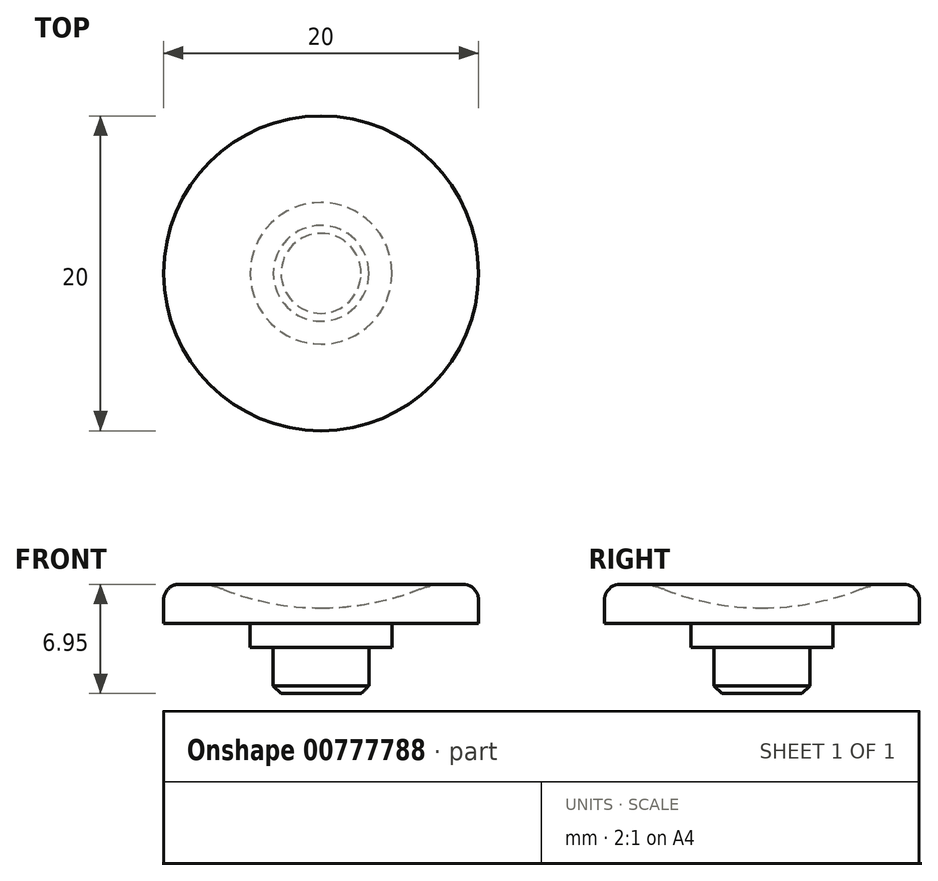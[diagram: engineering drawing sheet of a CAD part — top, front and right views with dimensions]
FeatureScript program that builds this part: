
annotation { "Feature Type Name" : "Feature", "Feature Type Description" : "" }
export const myFeature = defineFeature(function(context is Context, id is Id, definition is map)
    precondition{}
    {
        {
            var Q0;
            Q0=qCreatedBy(makeId("Front.planeOp"),FACE);
            var sketch = newSketch(context, id + "F0", { "sketchPlane" : qUnion([Q0])});
            skLineSegment(sketch, "E0", {"start": v(0, 0) * mm, "end": v(3.04, 0) * mm});
            skLineSegment(sketch, "E1", {"start": v(3.04, 0) * mm, "end": v(3.04, 2.95) * mm});
            skLineSegment(sketch, "E2", {"start": v(3.04, 2.95) * mm, "end": v(4.5, 2.95) * mm});
            skLineSegment(sketch, "E3", {"start": v(4.5, 2.95) * mm, "end": v(4.5, 4.45) * mm});
            skLineSegment(sketch, "E4", {"start": v(0, 0) * mm, "end": v(0, 5.45) * mm});
            skLineSegment(sketch, "E5", {"start": v(4.5, 4.45) * mm, "end": v(10, 4.45) * mm});
            skLineSegment(sketch, "E6", {"start": v(10, 4.45) * mm, "end": v(10, 6.95) * mm});
            skLineSegment(sketch, "E7", {"start": v(10, 6.95) * mm, "end": v(7, 6.95) * mm});
            skArc(sketch, "E8", {"start": v(0, 5.45) * mm, "mid": v(3.58, 5.83) * mm, "end": v(7, 6.95) * mm});
            skLineSegment(sketch, "E9", {"start": v(0, 10.08) * mm, "end": v(0, -2.44) * mm, "construction": true});
            skSolve(sketch);
        }
        {
            var Q0;
            Q0 = qSketchRegion(id + "F0", true);
            var Q1;
            Q1=sQuery(id+"F0.wireOp",EDGE,"E9");
            revolve(context, id + "F1", {"surfaceOperationType" : NewSurfaceOperationType.NEW, "entities" : qUnion([Q0]), "axis" : qUnion([Q1]), "revolveType" : RevolveType.FULL});
        }
        {
            var Q0;
            Q0=makeQuery(id+"F1.opRevolve","SWEPT_EDGE",EDGE,{"disambiguationData":[OSD([sQuery(id+"F0.wireOp",EDGE,"E7"),sQuery(id+"F0.wireOp",EDGE,"E8")])]});
            fillet(context, id + "F2", {"entities" : qUnion([Q0]), "radius" : 5 * mm, "tangentPropagation" : true, "allowEdgeOverflow" : false});
        }
        {
            var Q0;
            Q0=makeQuery(id+"F1.opRevolve","SWEPT_EDGE",EDGE,{"disambiguationData":[OSD([sQuery(id+"F0.wireOp",EDGE,"E6"),sQuery(id+"F0.wireOp",EDGE,"E7")])]});
            fillet(context, id + "F3", {"entities" : qUnion([Q0]), "radius" : 1 * mm, "tangentPropagation" : true, "allowEdgeOverflow" : false});
        }
        {
            var Q0;
            Q0=makeQuery(id+"F1.opRevolve","SWEPT_EDGE",EDGE,{"disambiguationData":[OSD([sQuery(id+"F0.wireOp",EDGE,"E0"),sQuery(id+"F0.wireOp",EDGE,"E1")])]});
            chamfer(context, id + "F4", {"entities" : qUnion([Q0]), "width" : .5 * mm, "tangentPropagation" : true});
        }
    });
